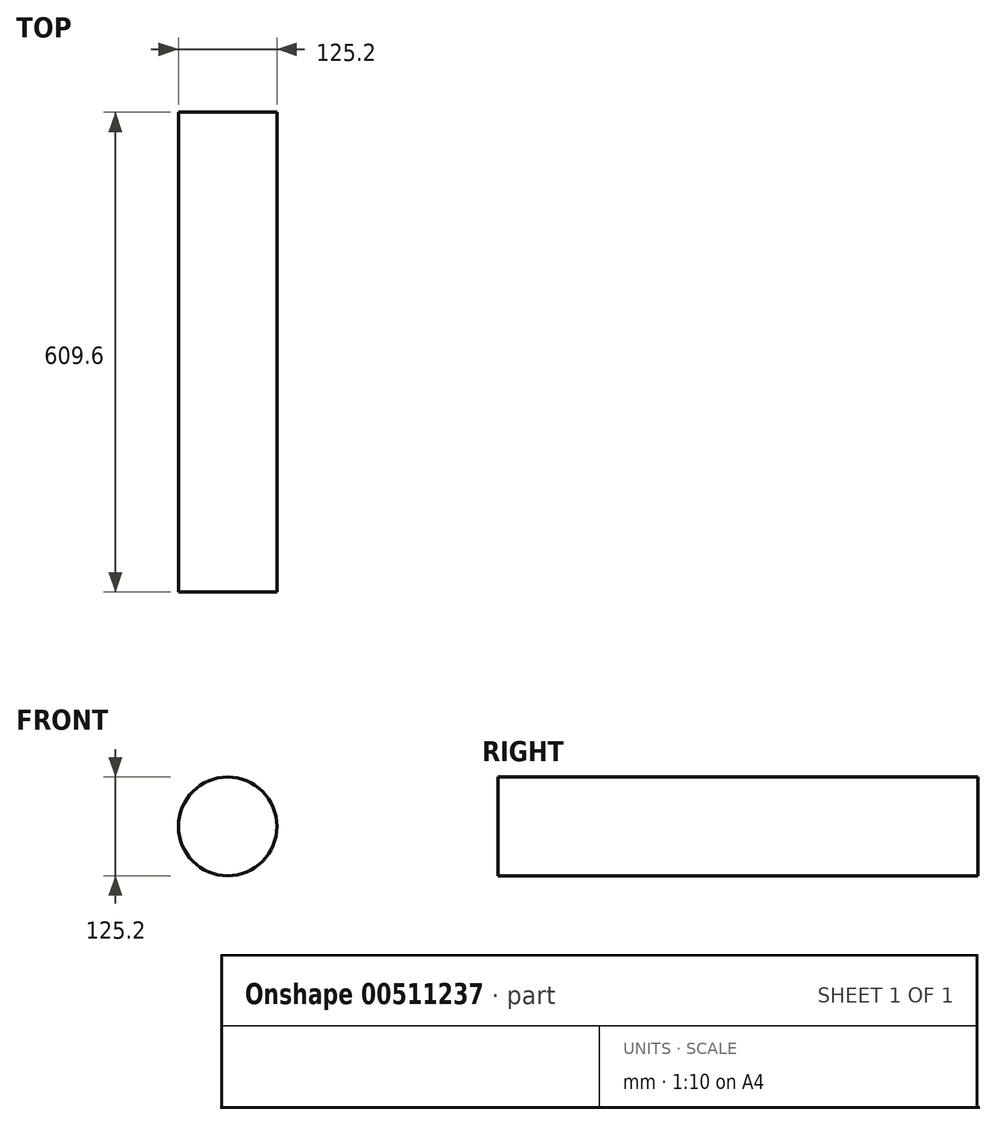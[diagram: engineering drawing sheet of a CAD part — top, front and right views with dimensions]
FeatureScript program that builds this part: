
annotation { "Feature Type Name" : "Feature", "Feature Type Description" : "" }
export const myFeature = defineFeature(function(context is Context, id is Id, definition is map)
    precondition{}
    {
        {
            var Q0;
            Q0=qCreatedBy(makeId("Front.planeOp"),FACE);
            var sketch = newSketch(context, id + "F0", { "sketchPlane" : qUnion([Q0])});
            skCircle(sketch, "E0", {"center": v(0, 0) * mm, "radius": 62.6 * mm});
            skSolve(sketch);
        }
        {
            var Q0;
            Q0 = qSketchRegion(id + "F0", true);
            extrude(context, id + "F1", {"entities" : qUnion([Q0]), "depth" : 609.6 * mm});
        }
    });
